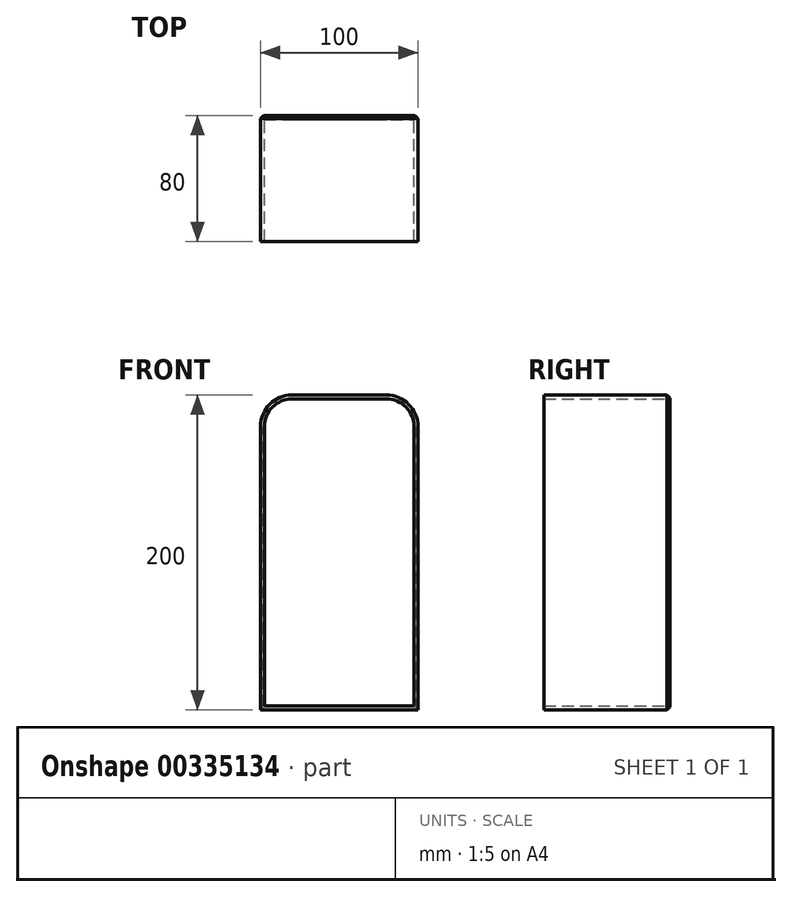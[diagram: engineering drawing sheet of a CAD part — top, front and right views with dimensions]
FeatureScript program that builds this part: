
annotation { "Feature Type Name" : "Feature", "Feature Type Description" : "" }
export const myFeature = defineFeature(function(context is Context, id is Id, definition is map)
    precondition{}
    {
        {
            var Q0;
            Q0=qCreatedBy(makeId("Front.planeOp"),FACE);
            var sketch = newSketch(context, id + "F0", { "sketchPlane" : qUnion([Q0])});
            skLineSegment(sketch, "E0.bottom", {"start": v(-30, 100) * mm, "end": v(30, 100) * mm});
            skLineSegment(sketch, "E0.top", {"start": v(-50, -100) * mm, "end": v(50, -100) * mm});
            skLineSegment(sketch, "E0.left", {"start": v(-50, 80) * mm, "end": v(-50, -100) * mm});
            skLineSegment(sketch, "E0.right", {"start": v(50, 80) * mm, "end": v(50, -100) * mm});
            skPoint(sketch, "E1.visualSharp", {"position": v(-50, 100) * mm});
            skArc(sketch, "E1.filletArc", {"start": v(-30, 100) * mm, "mid": v(-44.14, 94.14) * mm, "end": v(-50, 80) * mm});
            skPoint(sketch, "E2.visualSharp", {"position": v(50, 100) * mm});
            skArc(sketch, "E2.filletArc", {"start": v(50, 80) * mm, "mid": v(44.14, 94.14) * mm, "end": v(30, 100) * mm});
            skSolve(sketch);
        }
        {
            var Q0;
            Q0=makeQuery(id+"F0.imprint","IMPRINT",FACE,{"disambiguationData":[TD([[makeQuery(id+"F0.imprint","IMPRINT",EDGE,{"derivedFrom":sQuery(id+"F0.wireOp",EDGE,"E0.bottom")}),-1.0]])]});
            extrude(context, id + "F1", {"entities" : qUnion([Q0]), "depth" : 80 * mm});
        }
        {
            var Q0;
            Q0=makeQuery(id+"F1.opExtrude","CAP_FACE",FACE,{"disambiguationData":[OSD([sQuery(id+"F0.wireOp",EDGE,"E0.bottom"),sQuery(id+"F0.wireOp",EDGE,"E0.top"),sQuery(id+"F0.wireOp",EDGE,"E0.left"),sQuery(id+"F0.wireOp",EDGE,"E0.right"),sQuery(id+"F0.wireOp",EDGE,"E1.filletArc"),sQuery(id+"F0.wireOp",EDGE,"E2.filletArc")])],"isStart":false});
            shell(context, id + "F2", {"entities" : qUnion([Q0]), "thickness" : 2.5 * mm});
        }
        {
            var Q0;
            Q0=makeQuery(id+"F1.opExtrude","CAP_EDGE",EDGE,{"disambiguationData":[OSD([sQuery(id+"F0.wireOp",EDGE,"E0.right")])],"isStart":true});
            var Q1;
            Q1=makeQuery(id+"F1.opExtrude","CAP_FACE",FACE,{"disambiguationData":[OSD([sQuery(id+"F0.wireOp",EDGE,"E0.bottom"),sQuery(id+"F0.wireOp",EDGE,"E0.top"),sQuery(id+"F0.wireOp",EDGE,"E0.left"),sQuery(id+"F0.wireOp",EDGE,"E0.right"),sQuery(id+"F0.wireOp",EDGE,"E1.filletArc"),sQuery(id+"F0.wireOp",EDGE,"E2.filletArc")])],"isStart":true});
            chamfer(context, id + "F3", {"entities" : qUnion([Q0, Q1]), "width" : 2 * mm, "tangentPropagation" : true});
        }
    });
